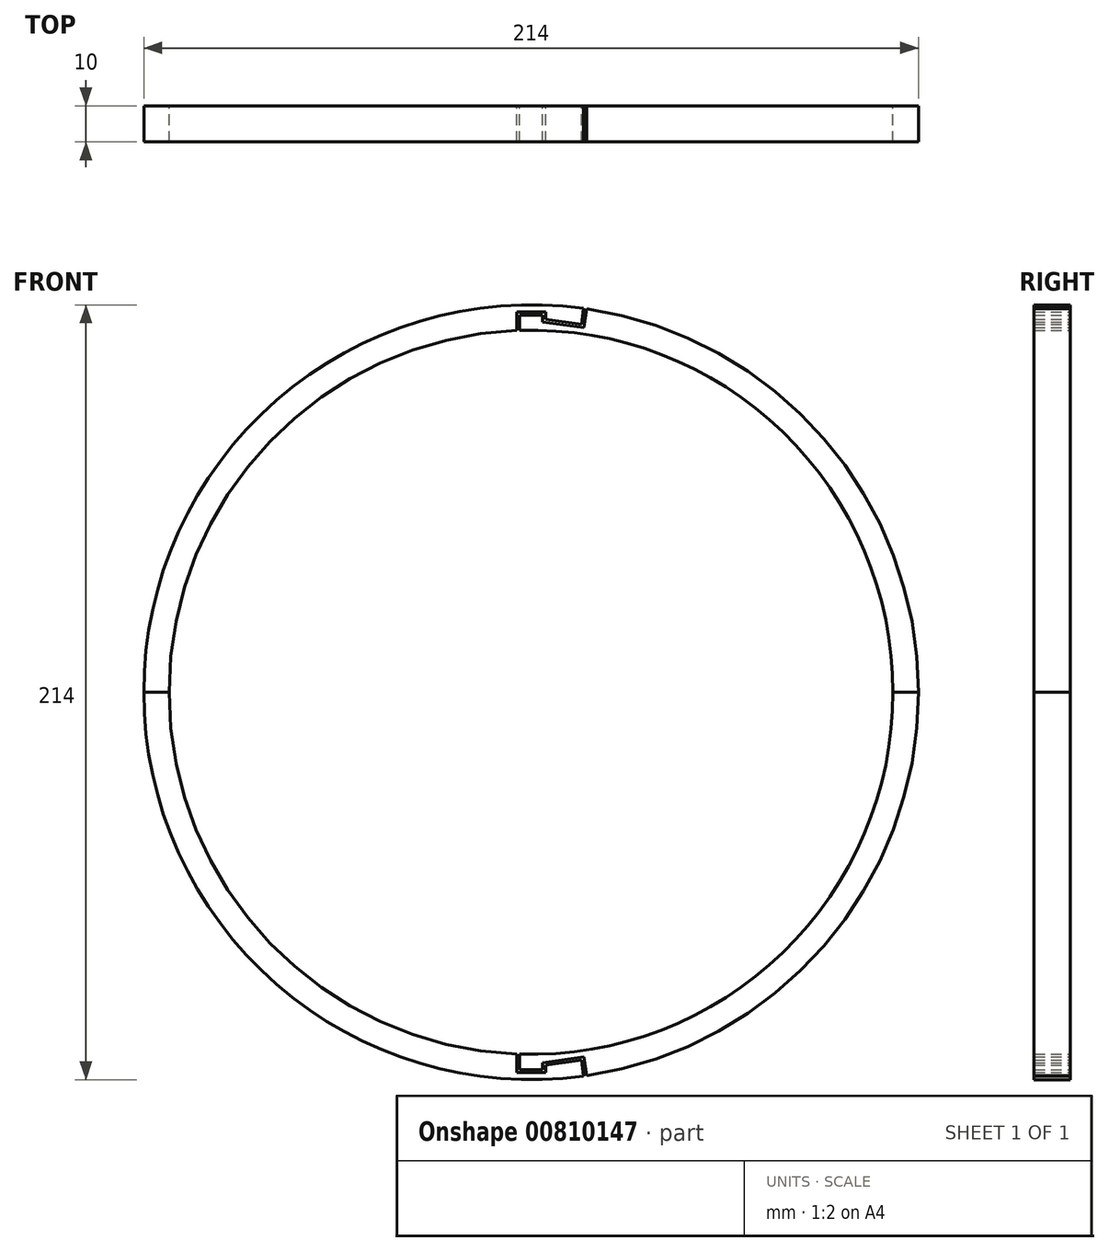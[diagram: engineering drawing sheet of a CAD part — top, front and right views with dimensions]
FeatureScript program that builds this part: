
annotation { "Feature Type Name" : "Feature", "Feature Type Description" : "" }
export const myFeature = defineFeature(function(context is Context, id is Id, definition is map)
    precondition{}
    {
        {
            var Q0;
            Q0=qCreatedBy(makeId("Front.planeOp"),FACE);
            var sketch = newSketch(context, id + "F0", { "sketchPlane" : qUnion([Q0])});
            skLineSegment(sketch, "E0", {"start": v(4, 103) * mm, "end": v(4, 105) * mm});
            skLineSegment(sketch, "E1", {"start": v(4, 105) * mm, "end": v(-4, 105) * mm});
            skLineSegment(sketch, "E2", {"start": v(-4, 105) * mm, "end": v(-4, 99.92) * mm});
            skArc(sketch, "E3", {"start": v(-4, 99.92) * mm, "mid": v(-72.11, 69.28) * mm, "end": v(-100, 0) * mm});
            skLineSegment(sketch, "E4", {"start": v(-100, 0) * mm, "end": v(-107, 0) * mm});
            skArc(sketch, "E5", {"start": v(-107, 0) * mm, "mid": v(-70.35, 80.63) * mm, "end": v(14.5, 106.01) * mm});
            skLineSegment(sketch, "E6", {"start": v(13.9, 101.64) * mm, "end": v(4, 103) * mm});
            skLineSegment(sketch, "E7", {"start": v(13.9, 101.64) * mm, "end": v(14.5, 106.01) * mm});
            skLineSegment(sketch, "E8", {"start": v(14.5, 106.01) * mm, "end": v(132.71, 89.84) * mm, "construction": true});
            skSolve(sketch);
        }
        {
            var Q0;
            Q0=qCreatedBy(makeId("Front.planeOp"),FACE);
            var sketch = newSketch(context, id + "F1", { "sketchPlane" : qUnion([Q0])});
            skArc(sketch, "E9", {"start": v(100, 0) * mm, "mid": v(69.57, 71.83) * mm, "end": v(-3.2, 99.95) * mm});
            skArc(sketch, "E10", {"start": v(107, 0) * mm, "mid": v(80.89, 70.04) * mm, "end": v(15.3, 105.9) * mm});
            skLineSegment(sketch, "E11.0", {"start": v(-3.2, 104.2) * mm, "end": v(-3.2, 99.95) * mm});
            skLineSegment(sketch, "E11.1", {"start": v(14.6, 100.74) * mm, "end": v(15.3, 105.9) * mm});
            skLineSegment(sketch, "E11.2", {"start": v(14.6, 100.74) * mm, "end": v(3.2, 102.3) * mm});
            skLineSegment(sketch, "E11.3", {"start": v(3.2, 102.3) * mm, "end": v(3.2, 104.2) * mm});
            skLineSegment(sketch, "E11.4", {"start": v(3.2, 104.2) * mm, "end": v(-3.2, 104.2) * mm});
            skLineSegment(sketch, "E12", {"start": v(100, 0) * mm, "end": v(107, 0) * mm});
            skSolve(sketch);
        }
        {
            var Q0;
            Q0=makeQuery(id+"F0.imprint","IMPRINT",FACE,{"disambiguationData":[TD([[makeQuery(id+"F0.imprint","IMPRINT",EDGE,{"derivedFrom":sQuery(id+"F0.wireOp",EDGE,"E0")}),-1.0]])]});
            extrude(context, id + "F2", {"entities" : qUnion([Q0]), "depth" : 10 * mm, "offsetDistance" : 25.4 * mm});
        }
        {
            var Q0;
            Q0=makeQuery(id+"F2.opExtrude","SWEPT_BODY",BODY,{"disambiguationData":[OSD([sQuery(id+"F0.wireOp",EDGE,"fUE91RAP-johp-kcSH-QWGp-oHSF55hXaz4T"),sQuery(id+"F0.wireOp",EDGE,"66MHe2oY-5wD2-DtNr-rrg0-H19Ir7GOMbSU"),sQuery(id+"F0.wireOp",EDGE,"BCibXuhN-k7rj-nNrd-M1AJ-3aUK4P34s18W"),sQuery(id+"F0.wireOp",EDGE,"SqVeZPUg-b4Ht-tPUu-rked-QgTnb0u2un3W"),sQuery(id+"F0.wireOp",EDGE,"FcjwYVc4-Gyei-Djis-8MqZ-jmBgjUwNKFDu"),sQuery(id+"F0.wireOp",EDGE,"E0"),sQuery(id+"F0.wireOp",EDGE,"E1"),sQuery(id+"F0.wireOp",EDGE,"E2"),sQuery(id+"F0.wireOp",EDGE,"E3"),sQuery(id+"F0.wireOp",EDGE,"E4")])]});
            var Q1;
            Q1=qCreatedBy(makeId("Top.planeOp"),FACE);
            mirror(context, id + "F3", {"entities" : qUnion([Q0]), "mirrorPlane" : qUnion([Q1])});
        }
        {
            var Q0;
            Q0=makeQuery(id+"F1.imprint","IMPRINT",FACE,{"disambiguationData":[TD([[makeQuery(id+"F1.imprint","IMPRINT",EDGE,{"derivedFrom":sQuery(id+"F1.wireOp",EDGE,"E9")}),-1.0]])]});
            extrude(context, id + "F4", {"entities" : qUnion([Q0]), "depth" : 10 * mm, "offsetDistance" : 25 * mm});
        }
        {
            var Q0;
            Q0=makeQuery(id+"F4.opExtrude","SWEPT_BODY",BODY,{"disambiguationData":[OSD([sQuery(id+"F1.wireOp",EDGE,"E9"),sQuery(id+"F1.wireOp",EDGE,"E10"),sQuery(id+"F1.wireOp",EDGE,"E11.0"),sQuery(id+"F1.wireOp",EDGE,"E11.1"),sQuery(id+"F1.wireOp",EDGE,"E11.2"),sQuery(id+"F1.wireOp",EDGE,"E11.3"),sQuery(id+"F1.wireOp",EDGE,"E11.4"),sQuery(id+"F1.wireOp",EDGE,"E12")])]});
            var Q1;
            Q1=qCreatedBy(makeId("Top.planeOp"),FACE);
            mirror(context, id + "F5", {"entities" : qUnion([Q0]), "mirrorPlane" : qUnion([Q1])});
        }
    });
